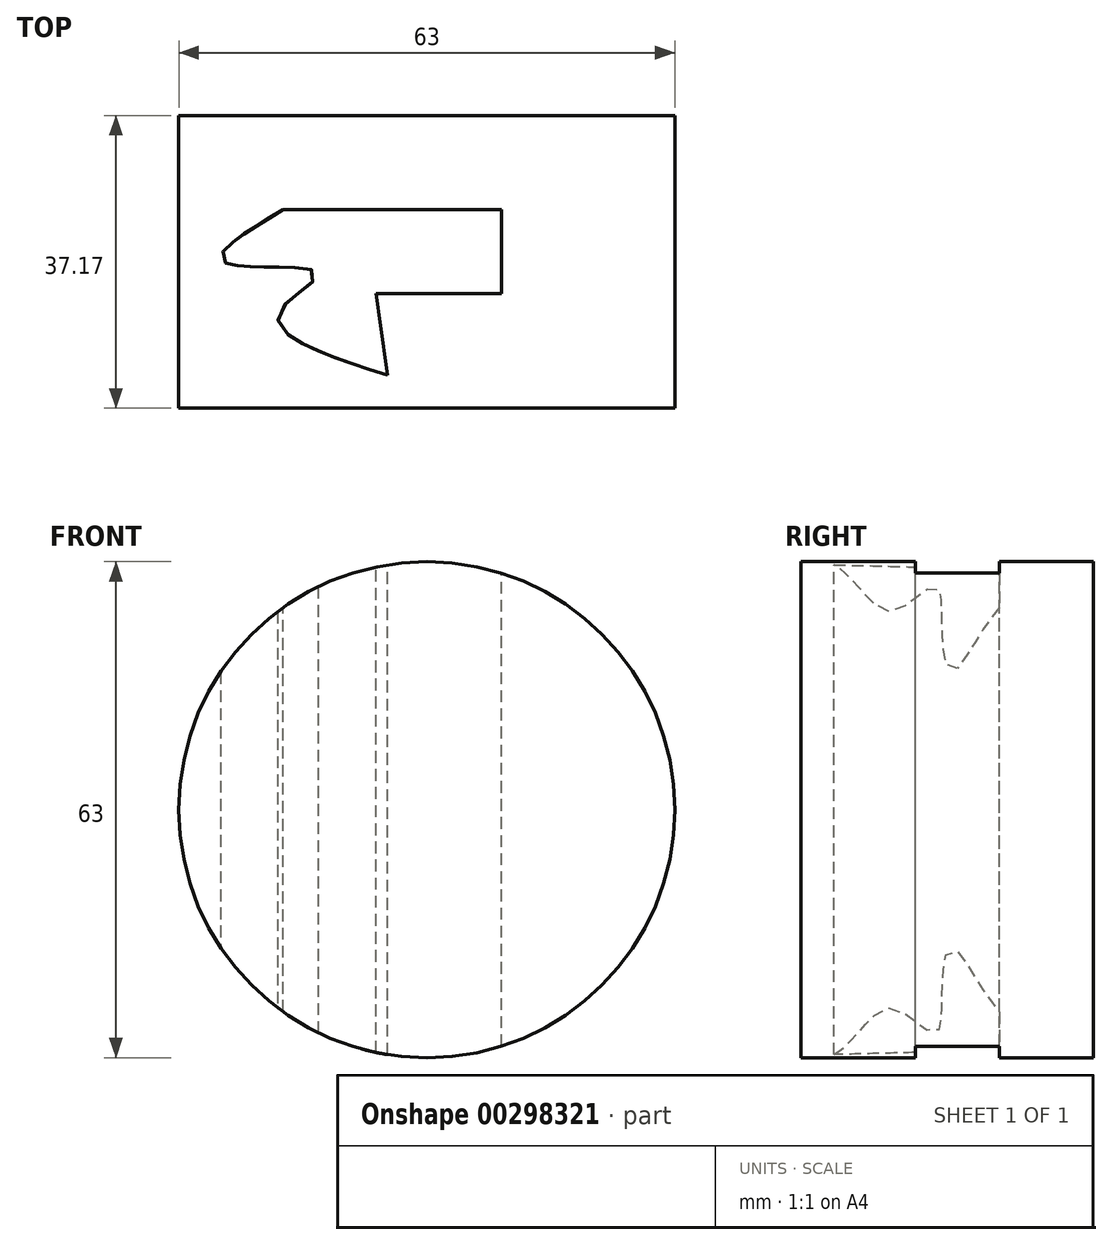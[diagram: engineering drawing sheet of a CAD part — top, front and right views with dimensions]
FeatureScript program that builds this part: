
annotation { "Feature Type Name" : "Feature", "Feature Type Description" : "" }
export const myFeature = defineFeature(function(context is Context, id is Id, definition is map)
    precondition{}
    {
        {
            var Q0;
            Q0=qCreatedBy(makeId("Front.planeOp"),FACE);
            var sketch = newSketch(context, id + "F0", { "sketchPlane" : qUnion([Q0])});
            skCircle(sketch, "E0", {"center": v(0, 0) * mm, "radius": 31.5 * mm});
            skSolve(sketch);
        }
        {
            var Q0;
            Q0 = qSketchRegion(id + "F0", true);
            extrude(context, id + "F1", {"entities" : qUnion([Q0]), "depth" : 37.17 * mm});
        }
        {
            var Q0;
            Q0=qCreatedBy(makeId("Top.planeOp"),FACE);
            cPlane(context, id + "F2", {"entities" : qUnion([Q0]), "cplaneType" : CPlaneType.OFFSET, "offset" : 84.06 * mm, "width" : 152.4 * mm, "height" : 152.4 * mm});
        }
        {
            var Q0;
            Q0=qCreatedBy(id+"F2.planeOp",FACE);
            var sketch = newSketch(context, id + "F3", { "sketchPlane" : qUnion([Q0])});
            skLineSegment(sketch, "E1", {"start": v(-18.24, -11.93) * mm, "end": v(9.48, -11.93) * mm});
            skLineSegment(sketch, "E2", {"start": v(9.48, -11.93) * mm, "end": v(9.48, -22.61) * mm});
            skLineSegment(sketch, "E3", {"start": v(9.48, -22.61) * mm, "end": v(-6.44, -22.61) * mm});
            skLineSegment(sketch, "E4", {"start": v(-6.44, -22.61) * mm, "end": v(-5, -32.97) * mm});
            skFitSpline(sketch, "E5", {"points": [v(-5, -32.97) * mm, v(-18.82, -25.14) * mm, v(-13.85, -19.97) * mm, v(-25.85, -18.57) * mm, v(-18.24, -11.93) * mm], "startDerivative": vector(-75.1, 24.36) * mm, "endDerivative": vector(58.53, 35.18) * mm});
            skSolve(sketch);
        }
        {
            var Q0;
            Q0 = qSketchRegion(id + "F3", true);
            extrude(context, id + "F4", {"entities" : qUnion([Q0]), "operationType" : NewBodyOperationType.REMOVE, "oppositeDirection" : true, "depth" : 140.4 * mm});
        }
    });
